# Revit family: Electrical_Equipment_Crown_ Power-Supply
name_source: partatom
category: Electrical Equipment
units: mm (PartAtom-declared; Revit-internal decimal feet)

## family parameters
Cut with Voids When Loaded = No
Host = Face
OmniClass Number = 23.80.30.11
OmniClass Title = Power Supply Devices
Panel Configuration = Two Columns, Circuits Across
Part Type = Panelboard
Room Calculation Point = No
Round Connector Dimension = Use Diameter
Shared = No

## types (1)
- Crowd Mics™
    Apparent Load = 18 VA
    Connector Description = Input 120V
    Default Elevation = 48 "
    Description = Crowd Mics™ Audience Engagement Solution
    Frequency = 50 Hz
    Housing Material = Biamp - Plastic - Black
    Input Voltage = 120 V
    Manufacturer = Biamp
    Max Power Consumption = 18 W
    Model = Crowd Mics™
    Number of Poles = 1
    Power Factor = 1
    Product Documentation Link = https://downloads.biamp.com
    Product Page URL = https://www.biamp.com
    Product data url = https://bimobject.com
    URL = https://www.biamp.com
    Version = 1

## geometry (parser evidence)
native form markers: Sweep x3
no freeform markers — native parametric forms only
